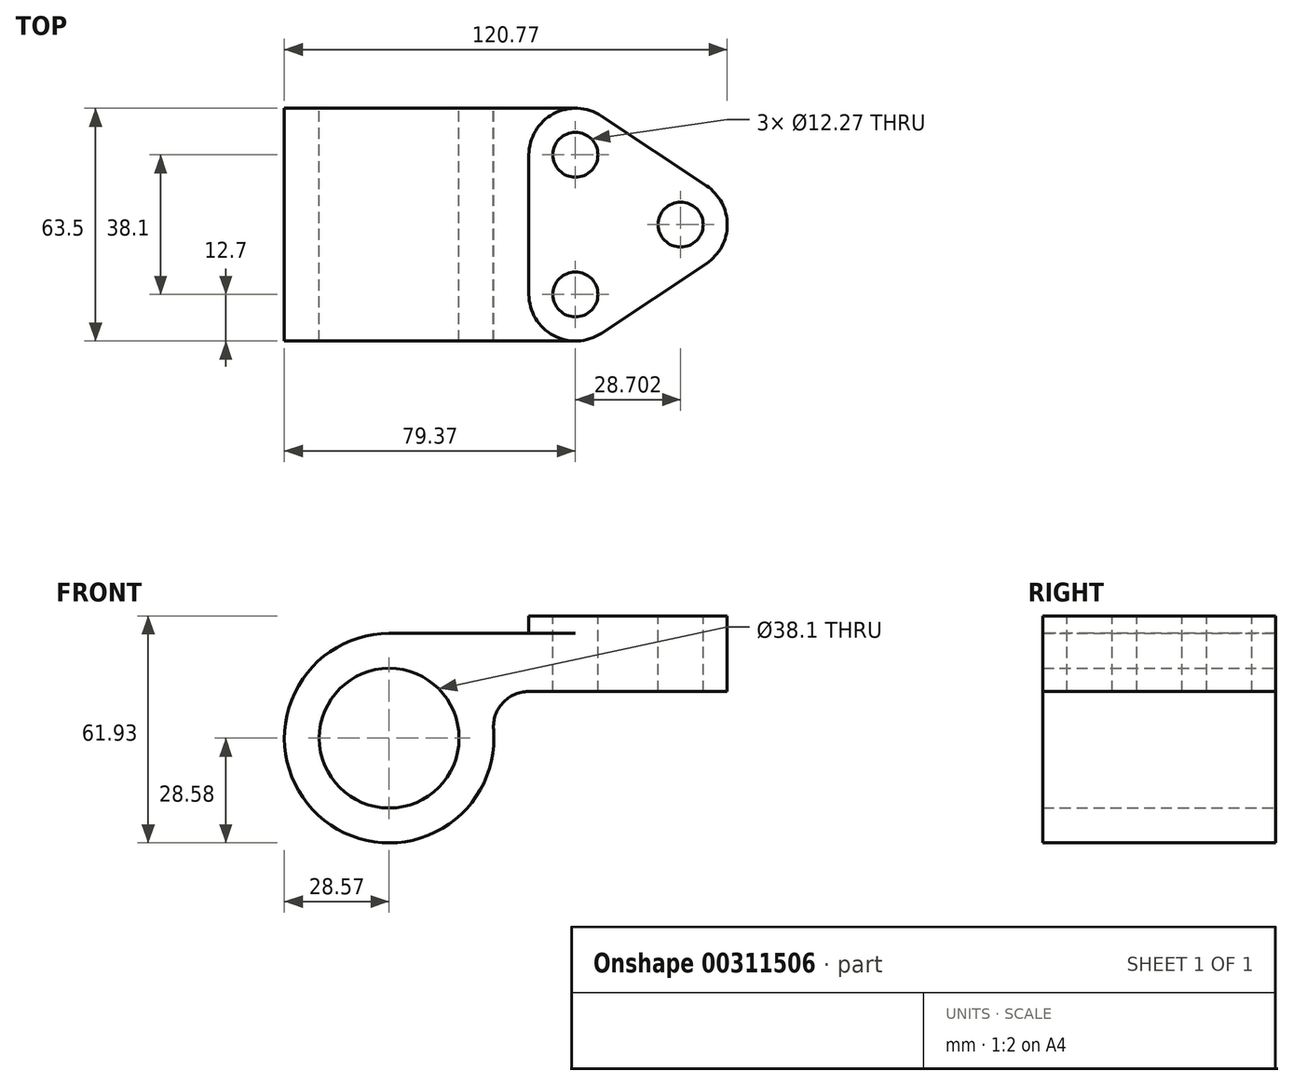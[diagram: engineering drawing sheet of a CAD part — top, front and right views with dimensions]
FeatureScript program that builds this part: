
annotation { "Feature Type Name" : "Feature", "Feature Type Description" : "" }
export const myFeature = defineFeature(function(context is Context, id is Id, definition is map)
    precondition{}
    {
        {
            var Q0;
            Q0=qCreatedBy(makeId("Front.planeOp"),FACE);
            var sketch = newSketch(context, id + "F0", { "sketchPlane" : qUnion([Q0])});
            skArc(sketch, "E0", {"start": v(0, 28.58) * mm, "mid": v(-19.35, -21.03) * mm, "end": v(28.48, 2.38) * mm});
            skLineSegment(sketch, "E1", {"start": v(0, 28.58) * mm, "end": v(79.5, 28.58) * mm});
            skCircle(sketch, "E2", {"center": v(0, 0) * mm, "radius": 19.05 * mm});
            skArc(sketch, "E3", {"start": v(37.97, 12.7) * mm, "mid": v(30.96, 9.62) * mm, "end": v(28.48, 2.38) * mm});
            skLineSegment(sketch, "E4", {"start": v(79.5, 28.58) * mm, "end": v(79.5, 12.7) * mm});
            skLineSegment(sketch, "E5", {"start": v(79.5, 12.7) * mm, "end": v(37.97, 12.7) * mm});
            skSolve(sketch);
        }
        {
            var Q0;
            Q0 = qSketchRegion(id + "F0", true);
            extrude(context, id + "F1", {"entities" : qUnion([Q0]), "depth" : 63.5 * mm});
        }
        {
            var Q0;
            Q0 = qSketchRegion(id + "F0", true);
            extrude(context, id + "F2", {"entities" : qUnion([Q0]), "operationType" : NewBodyOperationType.ADD, "depth" : 63.5 * mm});
        }
        {
            var Q0;
            Q0=makeQuery(id+"F1.opExtrude","SWEPT_FACE",FACE,{"disambiguationData":[OSD([sQuery(id+"F0.wireOp",EDGE,"E1")])]});
            var sketch = newSketch(context, id + "F3", { "sketchPlane" : qUnion([Q0])});
            skLineSegment(sketch, "E6.0.0", {"start": v(79.5, 0) * mm, "end": v(0, 0) * mm});
            skLineSegment(sketch, "E6.0.1", {"start": v(0, 0) * mm, "end": v(0, -63.5) * mm});
            skLineSegment(sketch, "E6.0.2", {"start": v(0, -63.5) * mm, "end": v(79.5, -63.5) * mm});
            skLineSegment(sketch, "E6.0.3", {"start": v(79.5, -63.5) * mm, "end": v(79.5, 0) * mm});
            skLineSegment(sketch, "E7", {"start": v(0, -31.75) * mm, "end": v(79.5, -31.75) * mm, "construction": true});
            skArc(sketch, "E8", {"start": v(57.82, -2.12) * mm, "mid": v(44.8, -1.5) * mm, "end": v(38.1, -12.7) * mm});
            skArc(sketch, "E9", {"start": v(38.1, -50.8) * mm, "mid": v(44.8, -62) * mm, "end": v(57.82, -61.38) * mm});
            skArc(sketch, "E10", {"start": v(79.5, -44.45) * mm, "mid": v(92.2, -31.75) * mm, "end": v(79.5, -19.05) * mm});
            skLineSegment(sketch, "E11", {"start": v(38.1, -12.7) * mm, "end": v(38.1, -50.8) * mm});
            skLineSegment(sketch, "E12", {"start": v(57.82, -61.38) * mm, "end": v(86.53, -42.33) * mm});
            skLineSegment(sketch, "E13", {"start": v(57.82, -2.12) * mm, "end": v(86.53, -21.17) * mm});
            skSolve(sketch);
        }
        {
            var Q0;
            {var subQ0=sQuery(id+"F3.wireOp",EDGE,"E10");var subQ1=sQuery(id+"F3.wireOp",EDGE,"E6.0.3");var subQ2=makeQuery(id+"F3.imprint","INTERSECT",VERTEX,{"disambiguationData":[OD(0.0)],"derivedFrom":[subQ1,subQ0]});Q0=makeQuery(id+"F3.imprint","IMPRINT",FACE,{"disambiguationData":[TD([[makeQuery(id+"F3.imprint","IMPRINT",EDGE,{"disambiguationData":[TD([[subQ2,1.0]])],"derivedFrom":subQ1}),-1.0]])]});}
            var Q1;
            {var subQ0=sQuery(id+"F3.wireOp",EDGE,"E10");var subQ1=sQuery(id+"F3.wireOp",EDGE,"E6.0.3");var subQ2=makeQuery(id+"F3.imprint","INTERSECT",VERTEX,{"disambiguationData":[OD(1.0)],"derivedFrom":[subQ1,subQ0]});Q1=makeQuery(id+"F3.imprint","IMPRINT",FACE,{"disambiguationData":[TD([[makeQuery(id+"F3.imprint","IMPRINT",EDGE,{"disambiguationData":[TD([[subQ2,-1.0]])],"derivedFrom":subQ1}),-1.0]])]});}
            var Q2;
            {var subQ0=sQuery(id+"F3.wireOp",EDGE,"E10");var subQ1=sQuery(id+"F3.wireOp",EDGE,"E6.0.3");var subQ2=makeQuery(id+"F3.imprint","INTERSECT",VERTEX,{"disambiguationData":[OD(0.0)],"derivedFrom":[subQ1,subQ0]});Q2=makeQuery(id+"F3.imprint","IMPRINT",FACE,{"disambiguationData":[TD([[makeQuery(id+"F3.imprint","IMPRINT",EDGE,{"disambiguationData":[TD([[subQ2,-1.0]])],"derivedFrom":subQ1}),-1.0]])]});}
            var Q3;
            {var subQ13=sQuery(id+"F3.wireOp",EDGE,"E11");Q3=makeQuery(id+"F3.imprint","IMPRINT",FACE,{"disambiguationData":[TD([[makeQuery(id+"F3.imprint","IMPRINT",EDGE,{"derivedFrom":subQ13}),1.0]])]});}
            extrude(context, id + "F4", {"entities" : qUnion([Q0, Q1, Q2, Q3]), "operationType" : NewBodyOperationType.ADD, "depth" : 4.78 * mm});
        }
        {
            var Q0;
            {var subQ2=sQuery(id+"F0.wireOp",EDGE,"E1");var subQ3=makeQuery(id+"F1.opExtrude","SWEPT_FACE",FACE,{"disambiguationData":[OSD([subQ2])]});var subQ4=sQuery(id+"F3.wireOp",EDGE,"E13");Q0=makeQuery(id+"F4.boolean.opBoolean","SPLIT",FACE,{"disambiguationData":[TD([makeQuery(id+"F4.opExtrude","SWEPT_FACE",FACE,{"disambiguationData":[OSD([subQ4])]})])],"derivedFrom":subQ3});}
            var Q1;
            {var subQ1=sQuery(id+"F3.wireOp",EDGE,"E12");var subQ3=sQuery(id+"F0.wireOp",EDGE,"E1");var subQ4=makeQuery(id+"F1.opExtrude","SWEPT_FACE",FACE,{"disambiguationData":[OSD([subQ3])]});Q1=makeQuery(id+"F4.boolean.opBoolean","SPLIT",FACE,{"disambiguationData":[TD([makeQuery(id+"F4.opExtrude","SWEPT_FACE",FACE,{"disambiguationData":[OSD([subQ1])]})])],"derivedFrom":subQ4});}
            extrude(context, id + "F5", {"entities" : qUnion([Q0, Q1]), "operationType" : NewBodyOperationType.REMOVE, "oppositeDirection" : true, "depth" : 25.4 * mm});
        }
        {
            var Q0;
            Q0=makeQuery(id+"F4.opExtrude","CAP_FACE",FACE,{"disambiguationData":[OSD([sQuery(id+"F3.wireOp",EDGE,"E8"),sQuery(id+"F3.wireOp",EDGE,"E9"),sQuery(id+"F3.wireOp",EDGE,"E10"),sQuery(id+"F3.wireOp",EDGE,"E11"),sQuery(id+"F3.wireOp",EDGE,"E12"),sQuery(id+"F3.wireOp",EDGE,"E13")])],"isStart":true});
            extrude(context, id + "F6", {"entities" : qUnion([Q0]), "operationType" : NewBodyOperationType.ADD, "depth" : 15.88 * mm});
        }
        {
            var Q0;
            Q0=makeQuery(id+"F4.opExtrude","CAP_FACE",FACE,{"disambiguationData":[OSD([sQuery(id+"F3.wireOp",EDGE,"E8"),sQuery(id+"F3.wireOp",EDGE,"E9"),sQuery(id+"F3.wireOp",EDGE,"E10"),sQuery(id+"F3.wireOp",EDGE,"E11"),sQuery(id+"F3.wireOp",EDGE,"E12"),sQuery(id+"F3.wireOp",EDGE,"E13")])],"isStart":false});
            var sketch = newSketch(context, id + "F7", { "sketchPlane" : qUnion([Q0])});
            skArc(sketch, "E14.0.0", {"start": v(38.1, -50.8) * mm, "mid": v(44.8, -62) * mm, "end": v(57.82, -61.38) * mm});
            skLineSegment(sketch, "E14.0.1", {"start": v(57.82, -61.38) * mm, "end": v(86.53, -42.33) * mm});
            skArc(sketch, "E14.0.2", {"start": v(86.53, -42.33) * mm, "mid": v(92.2, -31.75) * mm, "end": v(86.53, -21.17) * mm});
            skLineSegment(sketch, "E14.0.3", {"start": v(86.53, -21.17) * mm, "end": v(57.82, -2.12) * mm});
            skArc(sketch, "E14.0.4", {"start": v(57.82, -2.12) * mm, "mid": v(44.8, -1.5) * mm, "end": v(38.1, -12.7) * mm});
            skLineSegment(sketch, "E14.0.5", {"start": v(38.1, -12.7) * mm, "end": v(38.1, -50.8) * mm});
            skCircle(sketch, "E15", {"center": v(50.8, -12.7) * mm, "radius": 6.13 * mm});
            skCircle(sketch, "E16", {"center": v(50.8, -50.8) * mm, "radius": 6.13 * mm});
            skCircle(sketch, "E17", {"center": v(79.5, -31.75) * mm, "radius": 6.13 * mm});
            skSolve(sketch);
        }
        {
            var Q0;
            Q0=makeQuery(id+"F7.imprint","IMPRINT",FACE,{"disambiguationData":[TD([[makeQuery(id+"F7.imprint","IMPRINT",EDGE,{"derivedFrom":sQuery(id+"F7.wireOp",EDGE,"E15")}),1.0]])]});
            var Q1;
            Q1=makeQuery(id+"F7.imprint","IMPRINT",FACE,{"disambiguationData":[TD([[makeQuery(id+"F7.imprint","IMPRINT",EDGE,{"derivedFrom":sQuery(id+"F7.wireOp",EDGE,"E17")}),1.0]])]});
            var Q2;
            Q2=makeQuery(id+"F7.imprint","IMPRINT",FACE,{"disambiguationData":[TD([[makeQuery(id+"F7.imprint","IMPRINT",EDGE,{"derivedFrom":sQuery(id+"F7.wireOp",EDGE,"E16")}),1.0]])]});
            extrude(context, id + "F8", {"entities" : qUnion([Q0, Q1, Q2]), "operationType" : NewBodyOperationType.REMOVE, "oppositeDirection" : true, "depth" : 25.4 * mm});
        }
    });
